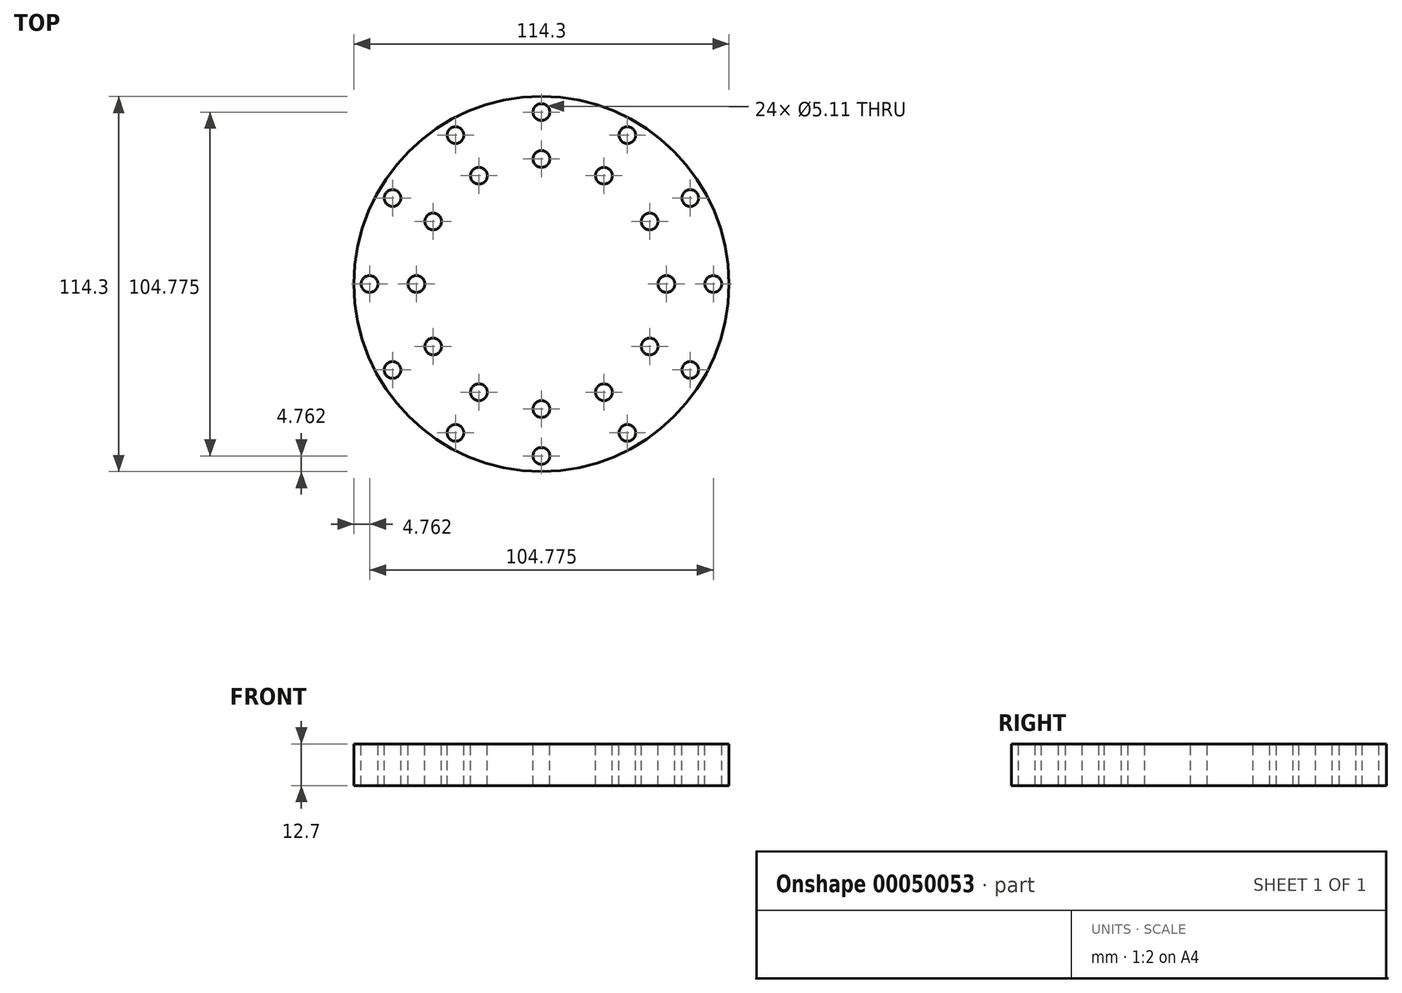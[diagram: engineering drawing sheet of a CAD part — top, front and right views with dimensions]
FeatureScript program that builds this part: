
annotation { "Feature Type Name" : "Feature", "Feature Type Description" : "" }
export const myFeature = defineFeature(function(context is Context, id is Id, definition is map)
    precondition{}
    {
        {
            var Q0;
            Q0=qCreatedBy(makeId("Top.planeOp"),FACE);
            var sketch = newSketch(context, id + "F0", { "sketchPlane" : qUnion([Q0])});
            skCircle(sketch, "E0", {"center": v(0, 0) * mm, "radius": 57.15 * mm});
            skSolve(sketch);
        }
        {
            var Q0;
            Q0 = qSketchRegion(id + "F0", true);
            extrude(context, id + "F1", {"entities" : qUnion([Q0]), "depth" : 12.7 * mm});
        }
        {
            var Q0;
            Q0=makeQuery(id+"F1.opExtrude","CAP_FACE",FACE,{"disambiguationData":[OSD([sQuery(id+"F0.wireOp",EDGE,"E0")])],"isStart":false});
            var sketch = newSketch(context, id + "F2", { "sketchPlane" : qUnion([Q0])});
            skCircle(sketch, "E1", {"center": v(-52.39, 0) * mm, "radius": 2.55 * mm});
            skSolve(sketch);
        }
        {
            var Q0;
            Q0 = qSketchRegion(id + "F2", true);
            extrude(context, id + "F3", {"entities" : qUnion([Q0]), "operationType" : NewBodyOperationType.REMOVE, "endBound" : BoundingType.UP_TO_NEXT, "oppositeDirection" : true, "depth" : 25.4 * mm});
        }
        {
            var Q0;
            Q0=qCreatedBy(makeId("Front.planeOp"),FACE);
            var sketch = newSketch(context, id + "F4", { "sketchPlane" : qUnion([Q0])});
            skLineSegment(sketch, "E2", {"start": v(0, 27.81) * mm, "end": v(0, -16.97) * mm});
            skSolve(sketch);
        }
        {
            var Q0;
            Q0=makeQuery(id+"F3.boolean.opBoolean","COPY",FACE,{"derivedFrom":makeQuery(id+"F3.opExtrude","SWEPT_FACE",FACE,{"disambiguationData":[OSD([sQuery(id+"F2.wireOp",EDGE,"E1")])]})});
            var Q1;
            Q1=sQuery(id+"F4.wireOp",EDGE,"E2");
            circularPattern(context, id + "F5", {"faces" : qUnion([Q0]), "axis" : qUnion([Q1]), "angle" : 360 * degree, "instanceCount" : 12, "equalSpace" : true, "patternType" : PatternType.FACE});
        }
        {
            var Q0;
            Q0=makeQuery(id+"F1.opExtrude","CAP_FACE",FACE,{"disambiguationData":[OSD([sQuery(id+"F0.wireOp",EDGE,"E0")])],"isStart":false});
            var sketch = newSketch(context, id + "F6", { "sketchPlane" : qUnion([Q0])});
            skCircle(sketch, "E3", {"center": v(0, 38.1) * mm, "radius": 2.55 * mm});
            skSolve(sketch);
        }
        {
            var Q0;
            Q0=makeQuery(id+"F6.imprint","IMPRINT",FACE,{"disambiguationData":[TD([[makeQuery(id+"F6.imprint","IMPRINT",EDGE,{"derivedFrom":sQuery(id+"F6.wireOp",EDGE,"E3")}),1.0]])]});
            extrude(context, id + "F7", {"entities" : qUnion([Q0]), "operationType" : NewBodyOperationType.REMOVE, "endBound" : BoundingType.UP_TO_NEXT, "oppositeDirection" : true, "depth" : 25.4 * mm});
        }
        {
            var Q0;
            Q0=makeQuery(id+"F7.boolean.opBoolean","COPY",FACE,{"derivedFrom":makeQuery(id+"F7.opExtrude","SWEPT_FACE",FACE,{"disambiguationData":[OSD([sQuery(id+"F6.wireOp",EDGE,"E3")])]})});
            var Q1;
            Q1=sQuery(id+"F4.wireOp",EDGE,"E2");
            circularPattern(context, id + "F8", {"faces" : qUnion([Q0]), "axis" : qUnion([Q1]), "angle" : 360 * degree, "instanceCount" : 12, "equalSpace" : true, "patternType" : PatternType.FACE});
        }
    });
